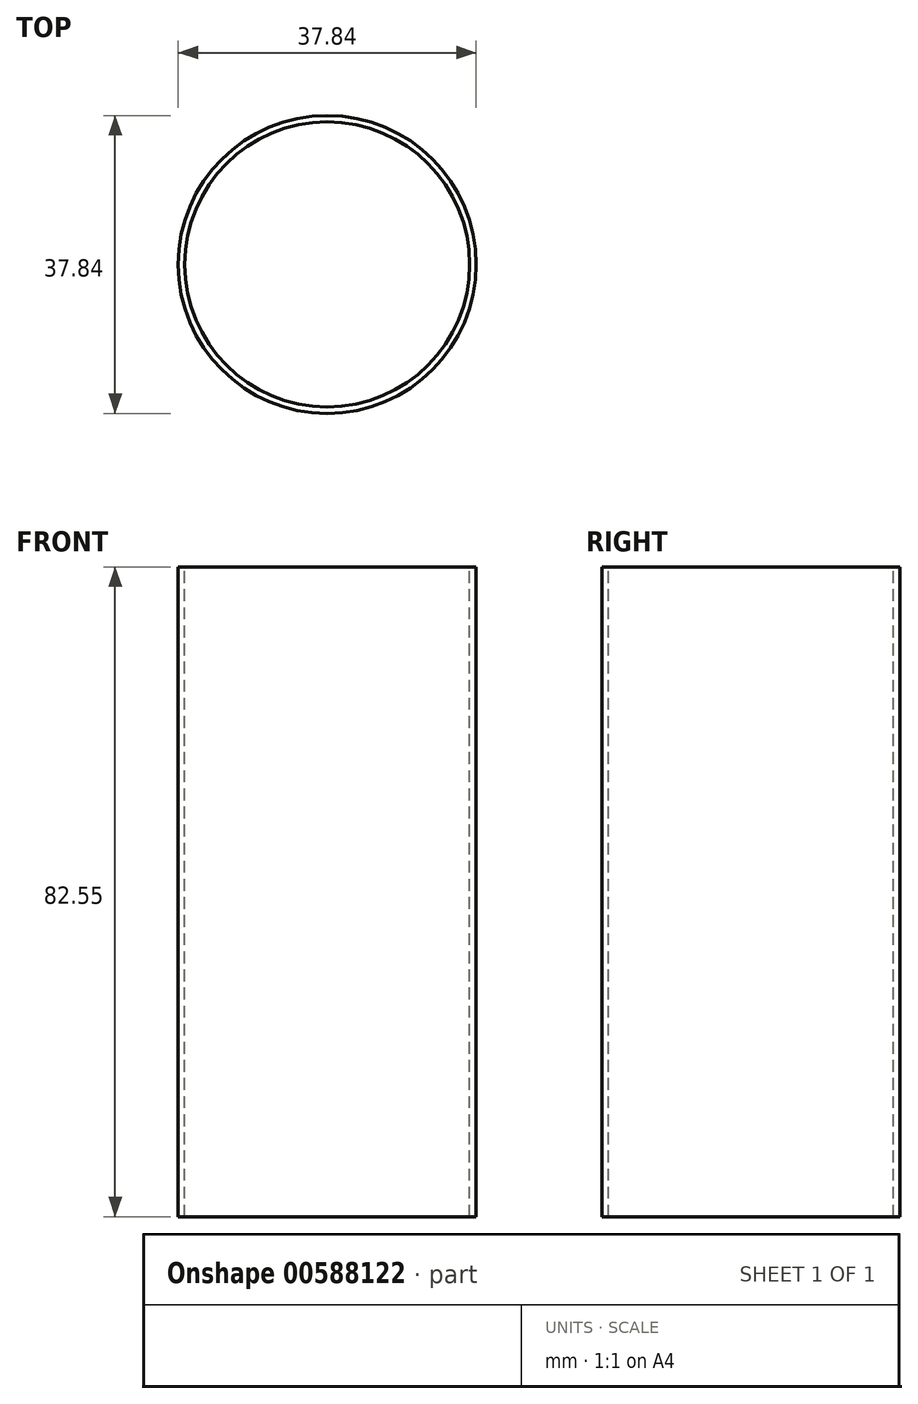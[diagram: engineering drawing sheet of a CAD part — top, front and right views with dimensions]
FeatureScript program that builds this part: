
annotation { "Feature Type Name" : "Feature", "Feature Type Description" : "" }
export const myFeature = defineFeature(function(context is Context, id is Id, definition is map)
    precondition{}
    {
        {
            var Q0;
            Q0=qCreatedBy(makeId("Top.planeOp"),FACE);
            var sketch = newSketch(context, id + "F0", { "sketchPlane" : qUnion([Q0])});
            skCircle(sketch, "E0", {"center": v(0, 0) * mm, "radius": 18.92 * mm});
            skCircle(sketch, "E1", {"center": v(0, 0) * mm, "radius": 18.11 * mm});
            skSolve(sketch);
        }
        {
            var Q0;
            Q0=sQuery(id+"F0.wireOp",EDGE,"E0");
            var Q1;
            Q1=sQuery(id+"F0.wireOp",EDGE,"E1");
            extrude(context, id + "F1", {"bodyType" : ToolBodyType.SURFACE, "surfaceEntities" : qUnion([Q0, Q1]), "depth" : 82.55 * mm, "offsetDistance" : 25.4 * mm});
        }
    });
